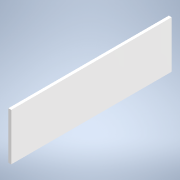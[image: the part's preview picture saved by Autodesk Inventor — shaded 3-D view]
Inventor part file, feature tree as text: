
AUTODESK INVENTOR PART (.ipt)
format: ipt  version: 2021.2 (Build 252289000, 289)  size: 90,624 bytes
history: native  units: in
note: dims shown in document units (in); Inventor stores cm internally (conversion verified against a paired STEP export)
features: extrude x1, sketch x1
ambient origin geometry x8: Origin, YZ Plane, XZ Plane, XY Plane, X Axis, Y Axis, Z Axis, Center Point
bodies: Solid1 (feature_tree)
feature tree (2):
  extrude  "Extrusion1"  Depth=0.75in
  sketch  "Sketch1"  dims[d0=0.075in d1=0.0in d2=0.75in d3=4.25in]
